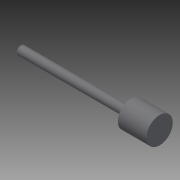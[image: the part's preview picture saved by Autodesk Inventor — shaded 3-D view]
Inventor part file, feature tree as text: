
AUTODESK INVENTOR PART (.ipt)
format: ipt  version: 2014 (Build 180170000, 170)  size: 123,904 bytes
history: native  units: in
note: dims shown in document units (in); Inventor stores cm internally (conversion verified against a paired STEP export)
features: other x49, revolve x2, sketch x2
ambient origin geometry x8: Origin, YZ Plane, XZ Plane, XY Plane, X Axis, Y Axis, Z Axis, Center Point
bodies: Solid1 (feature_tree)
feature tree (53):
  revolve  "Revolution1"  Angle=360.0deg
  revolve  "Revolution2"  [1 undecoded]
  other  "h1_XY"
  other  "h1_YZ"
  other  "h1_ZX"
  other  "h1_X"
  other  "h1_Y"
  other  "h1_Z"
  other  "h1_Center"
  other  "h2_XY"
  other  "h2_YZ"
  other  "h2_ZX"
  other  "h2_X"
  other  "h2_Y"
  other  "h2_Z"
  other  "h2_Center"
  other  "k1_XY"
  other  "k1_YZ"
  other  "k1_ZX"
  other  "k1_X"
  other  "k1_Y"
  other  "k1_Z"
  other  "k1_Center"
  other  "k2_XY"
  other  "k2_YZ"
  other  "k2_ZX"
  other  "k2_X"
  other  "k2_Y"
  other  "k2_Z"
  other  "k2_Center"
  other  "start_XY"
  other  "start_YZ"
  other  "start_ZX"
  other  "start_X"
  other  "start_Y"
  other  "start_Z"
  other  "start_Center"
  other  "to_prc_XY"
  other  "to_prc_YZ"
  other  "to_prc_ZX"
  other  "to_prc_X"
  other  "to_prc_Y"
  other  "to_prc_Z"
  other  "to_prc_Center"
  other  "to_rod_guide_XY"
  other  "to_rod_guide_YZ"
  other  "to_rod_guide_ZX"
  other  "to_rod_guide_X"
  other  "to_rod_guide_Y"
  other  "to_rod_guide_Z"
  other  "to_rod_guide_Center"
  sketch  "Sketch_5"  dims[d0=360.0deg d1=360.0deg]
  sketch  "Sketch_14"
note: 1 required parameter value undecoded (feature->parameter linkage not recoverable at this tier; creation-order binding heuristic only, values carry confidence <= 0.55)
